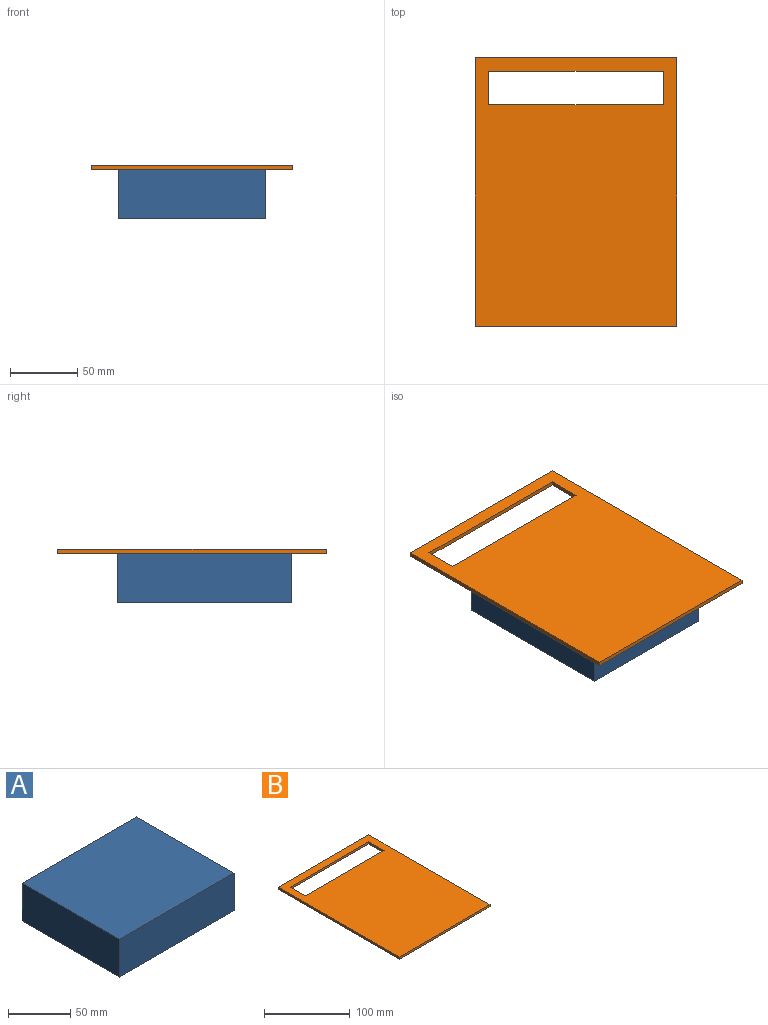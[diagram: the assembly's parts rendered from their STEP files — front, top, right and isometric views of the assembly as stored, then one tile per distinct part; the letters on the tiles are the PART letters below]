
ASSEMBLY  parts=2 mates=1
PART A: 11 faces, bbox 130x110x37 mm
  f0: plane 130x110mm, normal (0,0,-1), area 1404mm2, adj f1,f2,f3,f4,f6,f7,f8,f9
  f1: plane 130x37mm, normal (0,1,0), area 4810mm2, adj f0,f2,f4,f5
  f2: plane 110x37mm, normal (-1,0,0), area 4070mm2, adj f0,f1,f3,f5
  f3: plane 130x37mm, normal (0,-1,0), area 4810mm2, adj f0,f2,f4,f5
  f4: plane 110x37mm, normal (1,0,0), area 4070mm2, adj f0,f1,f3,f5
  f5: plane 130x110mm, normal (0,0,1), area 14300mm2, adj f1,f2,f3,f4
  f6: plane 124x34mm, normal (0,-1,0), area 4216mm2, adj f0,f7,f9,f10
  f7: plane 104x34mm, normal (1,0,0), area 3536mm2, adj f0,f6,f8,f10
  f8: plane 124x34mm, normal (0,1,0), area 4216mm2, adj f0,f7,f9,f10
  f9: plane 104x34mm, normal (-1,0,0), area 3536mm2, adj f0,f6,f8,f10
  f10: plane 124x104mm, normal (0,0,-1), area 12896mm2, adj f6,f7,f8,f9
PART B: 10 faces, bbox 150x200x3 mm
  f0: plane 150x3mm, normal (0,1,0), area 450mm2, adj f1,f7,f8,f9
  f1: plane 200x3mm, normal (-1,0,0), area 600mm2, adj f0,f2,f8,f9
  f2: plane 150x3mm, normal (0,-1,0), area 450mm2, adj f1,f7,f8,f9
  f3: plane 25x3mm, normal (1,0,0), area 75mm2, adj f4,f6,f8,f9
  f4: plane 130x3mm, normal (0,-1,0), area 390mm2, adj f3,f5,f8,f9
  f5: plane 25x3mm, normal (-1,0,0), area 75mm2, adj f4,f6,f8,f9
  f6: plane 130x3mm, normal (0,1,0), area 390mm2, adj f3,f5,f8,f9
  f7: plane 200x3mm, normal (1,0,0), area 600mm2, adj f0,f2,f8,f9
  f8: plane 200x150mm, normal (0,0,1), area 26750mm2, adj f0,f1,f2,f3,f4,f5,f6,f7
  f9: plane 200x150mm, normal (0,0,-1), area 26750mm2, adj f0,f1,f2,f3,f4,f5,f6,f7
PLACE A rot(axis=(0,0,-1),90deg) t=(-3.9,182.31,-80.74)mm
PLACE B t=(-61.11,3.74,-43.74)mm
MATE fastened A.f5 <-> B.f9  axis (0,0,1) through (-87.66,-14.24,-43.74)mm
